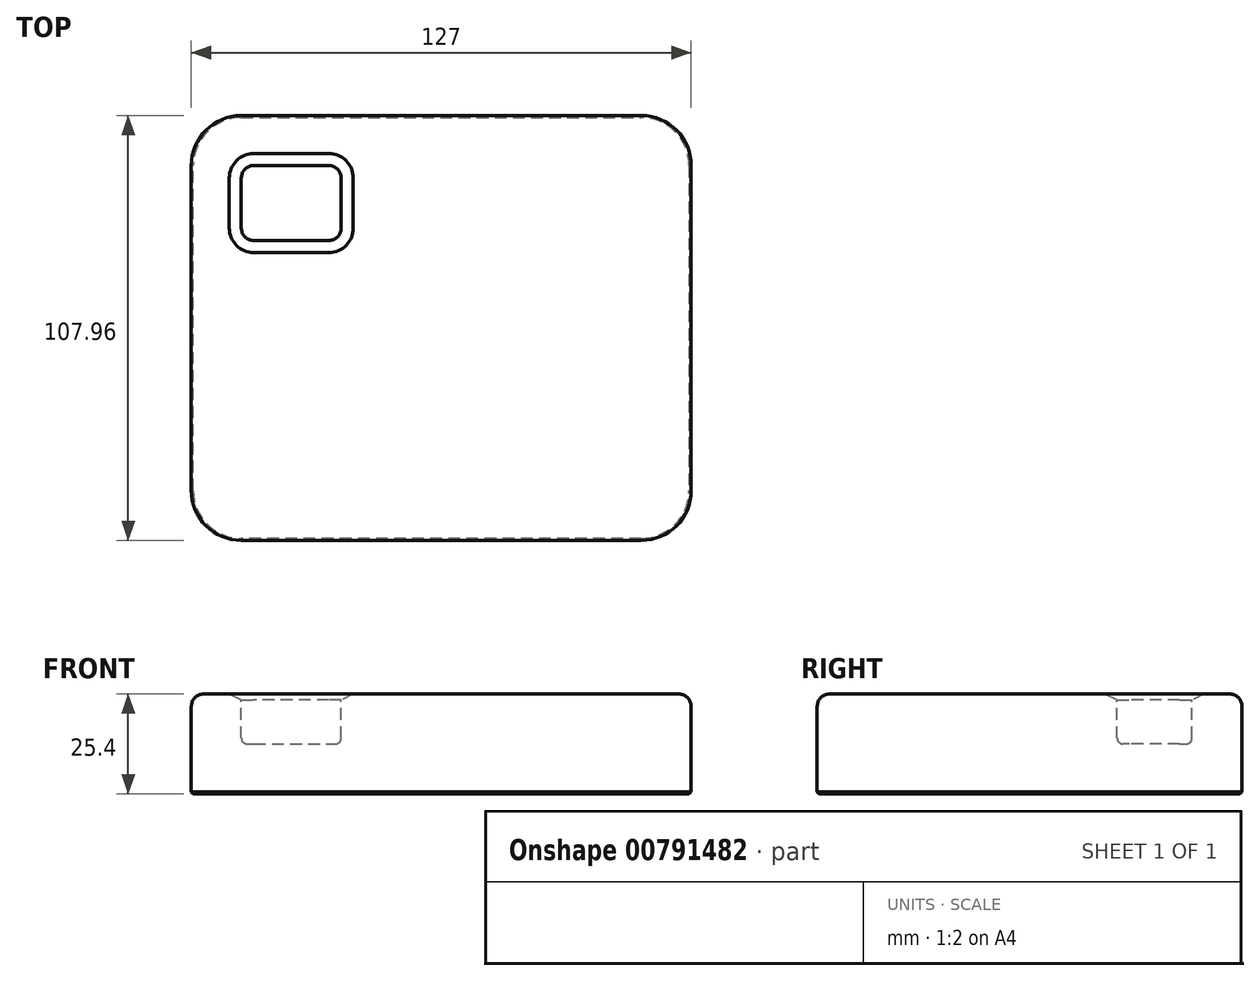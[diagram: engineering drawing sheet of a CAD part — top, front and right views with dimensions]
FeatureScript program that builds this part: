
annotation { "Feature Type Name" : "Feature", "Feature Type Description" : "" }
export const myFeature = defineFeature(function(context is Context, id is Id, definition is map)
    precondition{}
    {
        {
            var Q0;
            Q0=qCreatedBy(makeId("Top.planeOp"),FACE);
            var sketch = newSketch(context, id + "F0", { "sketchPlane" : qUnion([Q0])});
            skLineSegment(sketch, "E0.bottom", {"start": v(63.5, 53.98) * mm, "end": v(-63.5, 53.98) * mm});
            skLineSegment(sketch, "E0.top", {"start": v(63.5, -53.98) * mm, "end": v(-63.5, -53.98) * mm});
            skLineSegment(sketch, "E0.left", {"start": v(63.5, 53.98) * mm, "end": v(63.5, -53.98) * mm});
            skLineSegment(sketch, "E0.right", {"start": v(-63.5, 53.98) * mm, "end": v(-63.5, -53.98) * mm});
            skPoint(sketch, "E0.middle", {"position": v(0, 0) * mm});
            skSolve(sketch);
        }
        {
            var Q0;
            Q0=makeQuery(id+"F0.imprint","IMPRINT",FACE,{"disambiguationData":[TD([[makeQuery(id+"F0.imprint","IMPRINT",EDGE,{"derivedFrom":sQuery(id+"F0.wireOp",EDGE,"E0.bottom")}),1.0]])]});
            extrude(context, id + "F1", {"entities" : qUnion([Q0]), "depth" : 25.4 * mm});
        }
        {
            var Q0;
            Q0=makeQuery(id+"F1.opExtrude","CAP_FACE",FACE,{"disambiguationData":[OSD([sQuery(id+"F0.wireOp",EDGE,"E0.bottom"),sQuery(id+"F0.wireOp",EDGE,"E0.top"),sQuery(id+"F0.wireOp",EDGE,"E0.left"),sQuery(id+"F0.wireOp",EDGE,"E0.right")])],"isStart":false});
            var sketch = newSketch(context, id + "F2", { "sketchPlane" : qUnion([Q0])});
            skLineSegment(sketch, "E1.bottom", {"start": v(-50.8, 41.28) * mm, "end": v(-25.4, 41.28) * mm});
            skLineSegment(sketch, "E1.top", {"start": v(-50.8, 22.23) * mm, "end": v(-25.4, 22.23) * mm});
            skLineSegment(sketch, "E1.left", {"start": v(-50.8, 41.28) * mm, "end": v(-50.8, 22.23) * mm});
            skLineSegment(sketch, "E1.right", {"start": v(-25.4, 41.28) * mm, "end": v(-25.4, 22.23) * mm});
            skSolve(sketch);
        }
        {
            var Q0;
            Q0=makeQuery(id+"F2.imprint","IMPRINT",FACE,{"disambiguationData":[TD([[makeQuery(id+"F2.imprint","IMPRINT",EDGE,{"derivedFrom":sQuery(id+"F2.wireOp",EDGE,"E1.bottom")}),-1.0]])]});
            extrude(context, id + "F3", {"entities" : qUnion([Q0]), "operationType" : NewBodyOperationType.REMOVE, "oppositeDirection" : true, "depth" : 12.7 * mm});
        }
        {
            var Q0;
            Q0=makeQuery(id+"F3.boolean.opBoolean","COPY",EDGE,{"derivedFrom":makeQuery(id+"F3.opExtrude","SWEPT_EDGE",EDGE,{"disambiguationData":[OSD([sQuery(id+"F2.wireOp",EDGE,"E1.bottom"),sQuery(id+"F2.wireOp",EDGE,"E1.left")])]})});
            var Q1;
            Q1=makeQuery(id+"F3.boolean.opBoolean","COPY",EDGE,{"derivedFrom":makeQuery(id+"F3.opExtrude","SWEPT_EDGE",EDGE,{"disambiguationData":[OSD([sQuery(id+"F2.wireOp",EDGE,"E1.top"),sQuery(id+"F2.wireOp",EDGE,"E1.left")])]})});
            var Q2;
            Q2=makeQuery(id+"F3.boolean.opBoolean","COPY",EDGE,{"derivedFrom":makeQuery(id+"F3.opExtrude","SWEPT_EDGE",EDGE,{"disambiguationData":[OSD([sQuery(id+"F2.wireOp",EDGE,"E1.top"),sQuery(id+"F2.wireOp",EDGE,"E1.right")])]})});
            var Q3;
            Q3=makeQuery(id+"F3.boolean.opBoolean","COPY",EDGE,{"derivedFrom":makeQuery(id+"F3.opExtrude","SWEPT_EDGE",EDGE,{"disambiguationData":[OSD([sQuery(id+"F2.wireOp",EDGE,"E1.bottom"),sQuery(id+"F2.wireOp",EDGE,"E1.right")])]})});
            fillet(context, id + "F4", {"entities" : qUnion([Q0, Q1, Q2, Q3]), "radius" : 3.17 * mm, "tangentPropagation" : true, "allowEdgeOverflow" : false});
        }
        {
            var Q0;
            Q0=makeQuery(id+"F3.boolean.opBoolean","COPY",EDGE,{"derivedFrom":makeQuery(id+"F3.opExtrude","CAP_EDGE",EDGE,{"disambiguationData":[OSD([sQuery(id+"F2.wireOp",EDGE,"E1.top")])],"isStart":false})});
            fillet(context, id + "F5", {"entities" : qUnion([Q0]), "radius" : 1.52 * mm, "tangentPropagation" : true, "allowEdgeOverflow" : false});
        }
        {
            var Q0;
            Q0=makeQuery(id+"F1.opExtrude","SWEPT_EDGE",EDGE,{"disambiguationData":[OSD([sQuery(id+"F0.wireOp",EDGE,"E0.top"),sQuery(id+"F0.wireOp",EDGE,"E0.left")])]});
            var Q1;
            Q1=makeQuery(id+"F1.opExtrude","SWEPT_EDGE",EDGE,{"disambiguationData":[OSD([sQuery(id+"F0.wireOp",EDGE,"E0.bottom"),sQuery(id+"F0.wireOp",EDGE,"E0.left")])]});
            var Q2;
            Q2=makeQuery(id+"F1.opExtrude","SWEPT_EDGE",EDGE,{"disambiguationData":[OSD([sQuery(id+"F0.wireOp",EDGE,"E0.top"),sQuery(id+"F0.wireOp",EDGE,"E0.right")])]});
            var Q3;
            Q3=makeQuery(id+"F1.opExtrude","SWEPT_EDGE",EDGE,{"disambiguationData":[OSD([sQuery(id+"F0.wireOp",EDGE,"E0.bottom"),sQuery(id+"F0.wireOp",EDGE,"E0.right")])]});
            fillet(context, id + "F6", {"entities" : qUnion([Q0, Q1, Q2, Q3]), "radius" : 12.7 * mm, "tangentPropagation" : true, "allowEdgeOverflow" : false});
        }
        {
            var Q0;
            Q0=makeQuery(id+"F1.opExtrude","CAP_EDGE",EDGE,{"disambiguationData":[OSD([sQuery(id+"F0.wireOp",EDGE,"E0.top")])],"isStart":false});
            fillet(context, id + "F7", {"entities" : qUnion([Q0]), "radius" : 3.17 * mm, "tangentPropagation" : true, "allowEdgeOverflow" : false});
        }
        {
            var Q0;
            Q0=makeQuery(id+"F1.opExtrude","CAP_EDGE",EDGE,{"disambiguationData":[OSD([sQuery(id+"F0.wireOp",EDGE,"E0.top")])],"isStart":true});
            chamfer(context, id + "F8", {"entities" : qUnion([Q0]), "width" : 0.5 * mm, "tangentPropagation" : true});
        }
        {
            var Q0;
            Q0=makeQuery(id+"F3.boolean.opBoolean","COPY",EDGE,{"derivedFrom":makeQuery(id+"F3.opExtrude","CAP_EDGE",EDGE,{"disambiguationData":[OSD([sQuery(id+"F2.wireOp",EDGE,"E1.bottom")])],"isStart":true})});
            var Q1;
            Q1=makeQuery(id+"F3.boolean.opBoolean","COPY",FACE,{"derivedFrom":makeQuery(id+"F3.opExtrude","SWEPT_FACE",FACE,{"disambiguationData":[OSD([sQuery(id+"F2.wireOp",EDGE,"E1.left")])]})});
            var Q2;
            Q2=makeQuery(id+"F4.opFillet","BLEND_FACE",FACE,{"disambiguationData":[OSD([sQuery(id+"F2.wireOp",EDGE,"E1.bottom"),sQuery(id+"F2.wireOp",EDGE,"E1.left")])]});
            var Q3;
            Q3=makeQuery(id+"F3.boolean.opBoolean","COPY",FACE,{"derivedFrom":makeQuery(id+"F3.opExtrude","SWEPT_FACE",FACE,{"disambiguationData":[OSD([sQuery(id+"F2.wireOp",EDGE,"E1.bottom")])]})});
            var Q4;
            Q4=makeQuery(id+"F4.opFillet","BLEND_FACE",FACE,{"disambiguationData":[OSD([sQuery(id+"F2.wireOp",EDGE,"E1.bottom"),sQuery(id+"F2.wireOp",EDGE,"E1.right")])]});
            var Q5;
            Q5=makeQuery(id+"F3.boolean.opBoolean","COPY",FACE,{"derivedFrom":makeQuery(id+"F3.opExtrude","SWEPT_FACE",FACE,{"disambiguationData":[OSD([sQuery(id+"F2.wireOp",EDGE,"E1.right")])]})});
            var Q6;
            {var subQ0=sQuery(id+"F2.wireOp",EDGE,"E1.right");var subQ1=sQuery(id+"F2.wireOp",EDGE,"E1.top");Q6=makeQuery(id+"F5.opFillet","BLEND_EDGE",EDGE,{"blendedFrom":[makeQuery(id+"F4.opFillet","BLEND_EDGE",EDGE,{"blendedFrom":[makeQuery(id+"F3.boolean.opBoolean","COPY",EDGE,{"derivedFrom":makeQuery(id+"F3.opExtrude","SWEPT_EDGE",EDGE,{"disambiguationData":[OSD([subQ1,subQ0])]})}),makeQuery(id+"F3.boolean.opBoolean","COPY",FACE,{"derivedFrom":makeQuery(id+"F3.opExtrude","CAP_FACE",FACE,{"disambiguationData":[OSD([sQuery(id+"F2.wireOp",EDGE,"E1.bottom"),subQ1,sQuery(id+"F2.wireOp",EDGE,"E1.left"),subQ0])],"isStart":false})})],"blendedInto":[makeQuery(id+"F3.boolean.opBoolean","COPY",FACE,{"derivedFrom":makeQuery(id+"F3.opExtrude","CAP_FACE",FACE,{"disambiguationData":[OSD([sQuery(id+"F2.wireOp",EDGE,"E1.bottom"),subQ1,sQuery(id+"F2.wireOp",EDGE,"E1.left"),subQ0])],"isStart":false})})]}),makeQuery(id+"F4.opFillet","BLEND_FACE",FACE,{"disambiguationData":[OSD([subQ1,subQ0])]})],"blendedInto":[makeQuery(id+"F4.opFillet","BLEND_FACE",FACE,{"disambiguationData":[OSD([subQ1,subQ0])]})]});}
            var Q7;
            Q7=makeQuery(id+"F3.boolean.opBoolean","COPY",FACE,{"derivedFrom":makeQuery(id+"F3.opExtrude","SWEPT_FACE",FACE,{"disambiguationData":[OSD([sQuery(id+"F2.wireOp",EDGE,"E1.top")])]})});
            var Q8;
            Q8=makeQuery(id+"F4.opFillet","BLEND_FACE",FACE,{"disambiguationData":[OSD([sQuery(id+"F2.wireOp",EDGE,"E1.top"),sQuery(id+"F2.wireOp",EDGE,"E1.left")])]});
            chamfer(context, id + "F9", {"entities" : qUnion([Q0, Q1, Q2, Q3, Q4, Q5, Q6, Q7, Q8]), "chamferType" : ChamferType.TWO_OFFSETS, "width1" : 1.52 * mm, "oppositeDirection" : false, "width2" : 3.05 * mm, "tangentPropagation" : true});
        }
    });
